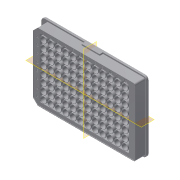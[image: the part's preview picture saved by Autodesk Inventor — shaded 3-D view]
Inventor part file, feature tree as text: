
AUTODESK INVENTOR PART (.ipt)
format: ipt  version: 2019 (Build 230136000, 136)  size: 5,472,256 bytes
history: native  units: in
note: dims shown in document units (in); Inventor stores cm internally (conversion verified against a paired STEP export)
features: plane x2
ambient origin geometry x8: Origin, YZ Plane, XZ Plane, XY Plane, X Axis, Y Axis, Z Axis, Center Point
bodies: Solid1 (feature_tree), Volumenkörper1 (feature_tree)
feature tree (2):
  plane  "Arbeitsebene1"
  plane  "Arbeitsebene2"
